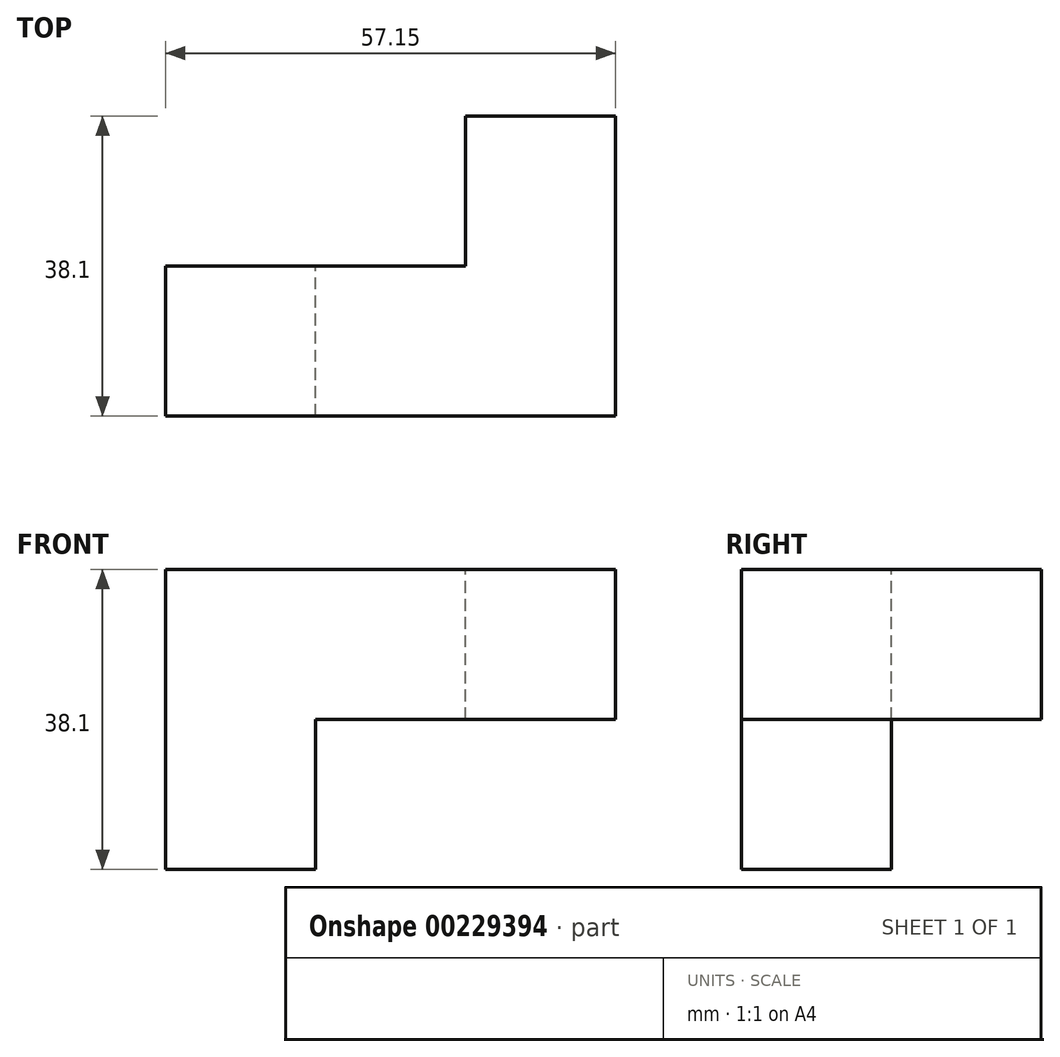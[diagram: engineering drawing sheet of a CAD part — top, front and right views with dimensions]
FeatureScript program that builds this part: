
annotation { "Feature Type Name" : "Feature", "Feature Type Description" : "" }
export const myFeature = defineFeature(function(context is Context, id is Id, definition is map)
    precondition{}
    {
        {
            var Q0;
            Q0=qCreatedBy(makeId("Front.planeOp"),FACE);
            var sketch = newSketch(context, id + "F0", { "sketchPlane" : qUnion([Q0])});
            skLineSegment(sketch, "E0.bottom", {"start": v(-2.32, -2.6) * mm, "end": v(54.83, -2.6) * mm});
            skLineSegment(sketch, "E0.top", {"start": v(-2.32, 16.45) * mm, "end": v(54.83, 16.45) * mm});
            skLineSegment(sketch, "E0.left", {"start": v(-2.32, -2.6) * mm, "end": v(-2.32, 16.45) * mm});
            skLineSegment(sketch, "E0.right", {"start": v(54.83, -2.6) * mm, "end": v(54.83, 16.45) * mm});
            skSolve(sketch);
        }
        {
            var Q0;
            Q0=makeQuery(id+"F0.imprint","IMPRINT",FACE,{"disambiguationData":[TD([[makeQuery(id+"F0.imprint","IMPRINT",EDGE,{"derivedFrom":sQuery(id+"F0.wireOp",EDGE,"E0.bottom")}),1.0]])]});
            extrude(context, id + "F1", {"entities" : qUnion([Q0]), "depth" : 19.05 * mm});
        }
        {
            var Q0;
            Q0=makeQuery(id+"FSQmz5JbGj1mDCK_1.boolean.opBoolean","MERGE",FACE,{"derivedFrom":[makeQuery(id+"F1.opExtrude","SWEPT_FACE",FACE,{"disambiguationData":[OSD([sQuery(id+"F0.wireOp",EDGE,"E0.bottom")])]}),makeQuery(id+"FSQmz5JbGj1mDCK_1.opExtrude","SWEPT_FACE",FACE,{"disambiguationData":[OSD([sQuery(id+"Ffho3R0e3bmfN8j_1.wireOp",EDGE,"8ZZvGZho-234g-glYk-VVZH-guR4EbsZ4S5A.bottom")])]})]});
            var sketch = newSketch(context, id + "F2", { "sketchPlane" : qUnion([Q0])});
            skLineSegment(sketch, "E1.bottom", {"start": v(-2.32, 19.05) * mm, "end": v(16.73, 19.05) * mm});
            skLineSegment(sketch, "E1.top", {"start": v(-2.32, 0) * mm, "end": v(16.73, 0) * mm});
            skLineSegment(sketch, "E1.left", {"start": v(-2.32, 19.05) * mm, "end": v(-2.32, 0) * mm});
            skLineSegment(sketch, "E1.right", {"start": v(16.73, 19.05) * mm, "end": v(16.73, 0) * mm});
            skSolve(sketch);
        }
        {
            var Q0;
            Q0=makeQuery(id+"F2.imprint","IMPRINT",FACE,{"disambiguationData":[TD([[makeQuery(id+"F2.imprint","IMPRINT",EDGE,{"derivedFrom":sQuery(id+"F2.wireOp",EDGE,"E1.bottom")}),-1.0]])]});
            extrude(context, id + "F3", {"entities" : qUnion([Q0]), "operationType" : NewBodyOperationType.ADD, "depth" : 19.05 * mm});
        }
        {
            var Q0;
            Q0=makeQuery(id+"F3.boolean.opBoolean","MERGE",FACE,{"derivedFrom":[makeQuery(id+"F1.opExtrude","CAP_FACE",FACE,{"disambiguationData":[OSD([sQuery(id+"F0.wireOp",EDGE,"E0.bottom"),sQuery(id+"F0.wireOp",EDGE,"E0.top"),sQuery(id+"F0.wireOp",EDGE,"E0.left"),sQuery(id+"F0.wireOp",EDGE,"E0.right")])],"isStart":true}),makeQuery(id+"F3.opExtrude","SWEPT_FACE",FACE,{"disambiguationData":[OSD([sQuery(id+"F2.wireOp",EDGE,"E1.top")])]})]});
            var sketch = newSketch(context, id + "F4", { "sketchPlane" : qUnion([Q0])});
            skLineSegment(sketch, "E2.bottom", {"start": v(-54.83, -2.6) * mm, "end": v(-35.78, -2.6) * mm});
            skLineSegment(sketch, "E2.top", {"start": v(-54.83, 16.45) * mm, "end": v(-35.78, 16.45) * mm});
            skLineSegment(sketch, "E2.left", {"start": v(-54.83, -2.6) * mm, "end": v(-54.83, 16.45) * mm});
            skLineSegment(sketch, "E2.right", {"start": v(-35.78, -2.6) * mm, "end": v(-35.78, 16.45) * mm});
            skSolve(sketch);
        }
        {
            var Q0;
            Q0=makeQuery(id+"F4.imprint","IMPRINT",FACE,{"disambiguationData":[TD([[makeQuery(id+"F4.imprint","IMPRINT",EDGE,{"derivedFrom":sQuery(id+"F4.wireOp",EDGE,"E2.bottom")}),-1.0]])]});
            extrude(context, id + "F5", {"entities" : qUnion([Q0]), "operationType" : NewBodyOperationType.ADD, "depth" : 19.05 * mm});
        }
    });
